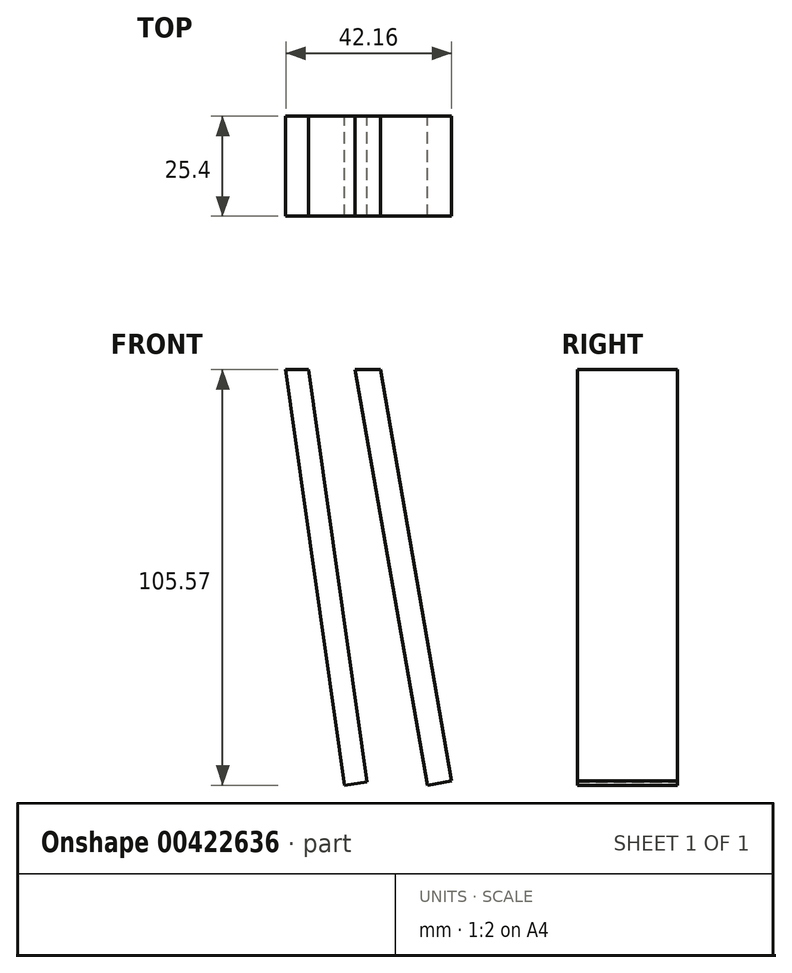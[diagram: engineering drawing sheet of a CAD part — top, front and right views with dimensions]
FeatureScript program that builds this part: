
annotation { "Feature Type Name" : "Feature", "Feature Type Description" : "" }
export const myFeature = defineFeature(function(context is Context, id is Id, definition is map)
    precondition{}
    {
        {
            var Q0;
            Q0=qCreatedBy(makeId("Front.planeOp"),FACE);
            var sketch = newSketch(context, id + "F0", { "sketchPlane" : qUnion([Q0])});
            skLineSegment(sketch, "E0", {"start": v(-68.5, 60.26) * mm, "end": v(-53.58, -45.31) * mm});
            skLineSegment(sketch, "E1", {"start": v(-53.58, -45.31) * mm, "end": v(-47.86, -44.5) * mm});
            skLineSegment(sketch, "E2", {"start": v(-47.86, -44.5) * mm, "end": v(-62.66, 60.26) * mm});
            skLineSegment(sketch, "E3", {"start": v(-62.66, 60.26) * mm, "end": v(-68.5, 60.26) * mm});
            skLineSegment(sketch, "E4", {"start": v(-50.87, 60.26) * mm, "end": v(-32.56, -45.31) * mm});
            skLineSegment(sketch, "E5", {"start": v(-32.56, -45.31) * mm, "end": v(-26.34, -44.23) * mm});
            skLineSegment(sketch, "E6", {"start": v(-26.34, -44.23) * mm, "end": v(-44.47, 60.26) * mm});
            skLineSegment(sketch, "E7", {"start": v(-44.47, 60.26) * mm, "end": v(-50.87, 60.26) * mm});
            skFitSpline(sketch, "E8", {"points": [v(-66.8, -55.57) * mm, v(-57.31, -70.47) * mm, v(-16.62, -65.5) * mm, v(-4.4, -38.58) * mm, v(-4.75, -40.37) * mm], "startDerivative": vector(20.28, -70.45) * mm, "endDerivative": vector(-6.6, -36.55) * mm});
            skSolve(sketch);
        }
        {
            var Q0;
            Q0 = qSketchRegion(id + "F0", true);
            extrude(context, id + "F1", {"entities" : qUnion([Q0]), "depth" : 25.4 * mm});
        }
        {
            var Q0;
            Q0=sQuery(id+"F0.wireOp",EDGE,"E8");
            extrude(context, id + "F2", {"bodyType" : ToolBodyType.SURFACE, "surfaceEntities" : qUnion([Q0]), "depth" : 25.4 * mm});
        }
    });
